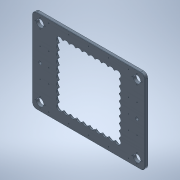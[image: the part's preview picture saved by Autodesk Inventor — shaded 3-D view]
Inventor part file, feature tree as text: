
AUTODESK INVENTOR PART (.ipt)
format: ipt  version: 2020.3 (Build 243373000, 373)  size: 553,472 bytes
history: native  units: in
note: dims shown in document units (in); Inventor stores cm internally (conversion verified against a paired STEP export)
features: hole x5, chamfer x3, extrude x2, fillet x2, pattern_linear x1, sketch x1
ambient origin geometry x8: Origin, YZ Plane, XZ Plane, XY Plane, X Axis, Y Axis, Z Axis, Center Point
bodies: Solid1 (feature_tree)
feature tree (14):
  extrude  "Extrusion1"  Depth=0.125in
  hole  "Hole1"  [1 undecoded]
  pattern_linear  "Rectangular Pattern1"  Spacing1=0.5in  [1 undecoded]
  extrude  "Extrusion2"  Depth=0.125in
  fillet  "Fillet1"  Radius=0.31in
  hole  "Hole2"  [1 undecoded]
  hole  "Hole3"  [1 undecoded]
  hole  "Hole4"  [1 undecoded]
  fillet  "Fillet4"  Radius=1.6929in
  chamfer  "Chamfer4"  Distance=3.5in
  chamfer  "Chamfer3"  Distance=3.5in
  hole  "Hole5"  [1 undecoded]
  chamfer  "Chamfer5"  Distance=14.75in
  sketch  "Sketch3"  dims[d0=5.085in d1=5.085in d2=19.75in d4=0.5in d5=0.0in d6=1.13in d7=0.75in d8=0.375in d9=0.25in d10=0.5635in d11=1.0in d12=0.8108in d13=3.937in d15=1.13in d16=3.937in d18=1.13in d19=0.31in d20=0.0in d21=0.125in d23=14.0in d24=17.0in d25=1.6929in d26=0.163in d27=0.394in d28=0.375in d29=0.25in d30=0.5635in d31=0.559in d32=0.8108in d33=1.2992in d34=0.394in d35=0.375in d36=0.25in d37=0.5635in d38=0.559in d39=0.8108in d56=0.163in d57=0.394in d58=0.375in d59=0.25in d60=0.5635in d61=0.559in d62=0.8108in d63=3.5in d64=3.5in d66=9.875in d70=14.75in d71=7.375in d72=8.5in d73=0.0in d74=0.0in d75=15.0in d76=1.0in d77=1.0in d80=0.75in d85=0.2in d86=0.125in d87=45.0deg d88=12.0in d89=6.0in d90=8.5in d91=8.5in d92=0.547in d93=0.5in d94=0.813in d95=0.5in d96=0.5635in d97=1.0in d98=0.8108in d104=1.5in d105=1.5in d106=4.25in d107=5.0in d108=0.3in d109=0.125in d110=45.0deg d111=0.05in d112=0.125in d113=45.0deg]
note: 6 required parameter values undecoded (feature->parameter linkage not recoverable at this tier; creation-order binding heuristic only, values carry confidence <= 0.55)
